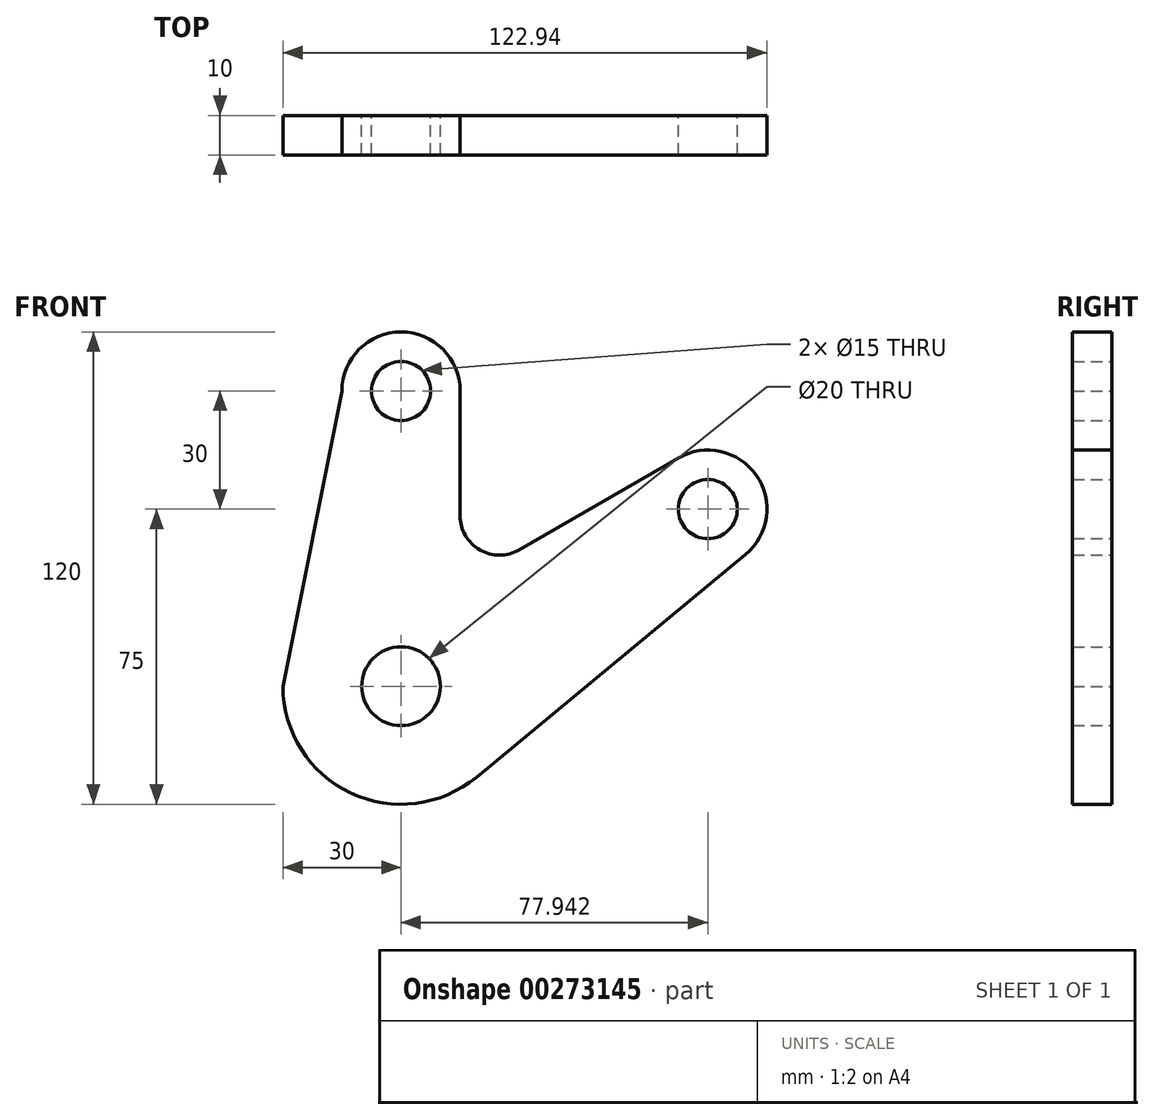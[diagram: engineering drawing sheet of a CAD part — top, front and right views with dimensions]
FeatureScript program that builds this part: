
annotation { "Feature Type Name" : "Feature", "Feature Type Description" : "" }
export const myFeature = defineFeature(function(context is Context, id is Id, definition is map)
    precondition{}
    {
        {
            var Q0;
            Q0=qCreatedBy(makeId("Front.planeOp"),FACE);
            var sketch = newSketch(context, id + "F0", { "sketchPlane" : qUnion([Q0])});
            skArc(sketch, "E0", {"start": v(-30, 0) * mm, "mid": v(-12.77, -27.14) * mm, "end": v(19.12, -23.12) * mm});
            skCircle(sketch, "E1", {"center": v(0, 0) * mm, "radius": 10 * mm});
            skCircle(sketch, "E2", {"center": v(0, 75) * mm, "radius": 7.5 * mm});
            skCircle(sketch, "E3", {"center": v(77.94, 45) * mm, "radius": 7.5 * mm});
            skArc(sketch, "E4", {"start": v(-15, 75) * mm, "mid": v(0, 90) * mm, "end": v(15, 75) * mm});
            skArc(sketch, "E5", {"start": v(70.44, 58) * mm, "mid": v(90.26, 53.56) * mm, "end": v(87.5, 33.44) * mm});
            skLineSegment(sketch, "E6", {"start": v(-30, 0) * mm, "end": v(-15, 75) * mm});
            skLineSegment(sketch, "E7", {"start": v(19.12, -23.12) * mm, "end": v(87.5, 33.44) * mm});
            skLineSegment(sketch, "E8", {"start": v(0, 0) * mm, "end": v(77.94, 45) * mm});
            skLineSegment(sketch, "E9", {"start": v(15, 75) * mm, "end": v(15, 43.3) * mm});
            skLineSegment(sketch, "E10", {"start": v(70.44, 58) * mm, "end": v(30, 34.64) * mm});
            skArc(sketch, "E11", {"start": v(15, 43.3) * mm, "mid": v(20, 34.64) * mm, "end": v(30, 34.64) * mm});
            skSolve(sketch);
        }
        {
            var Q0;
            Q0 = qSketchRegion(id + "F0", true);
            extrude(context, id + "F1", {"entities" : qUnion([Q0]), "depth" : 10 * mm});
        }
    });
